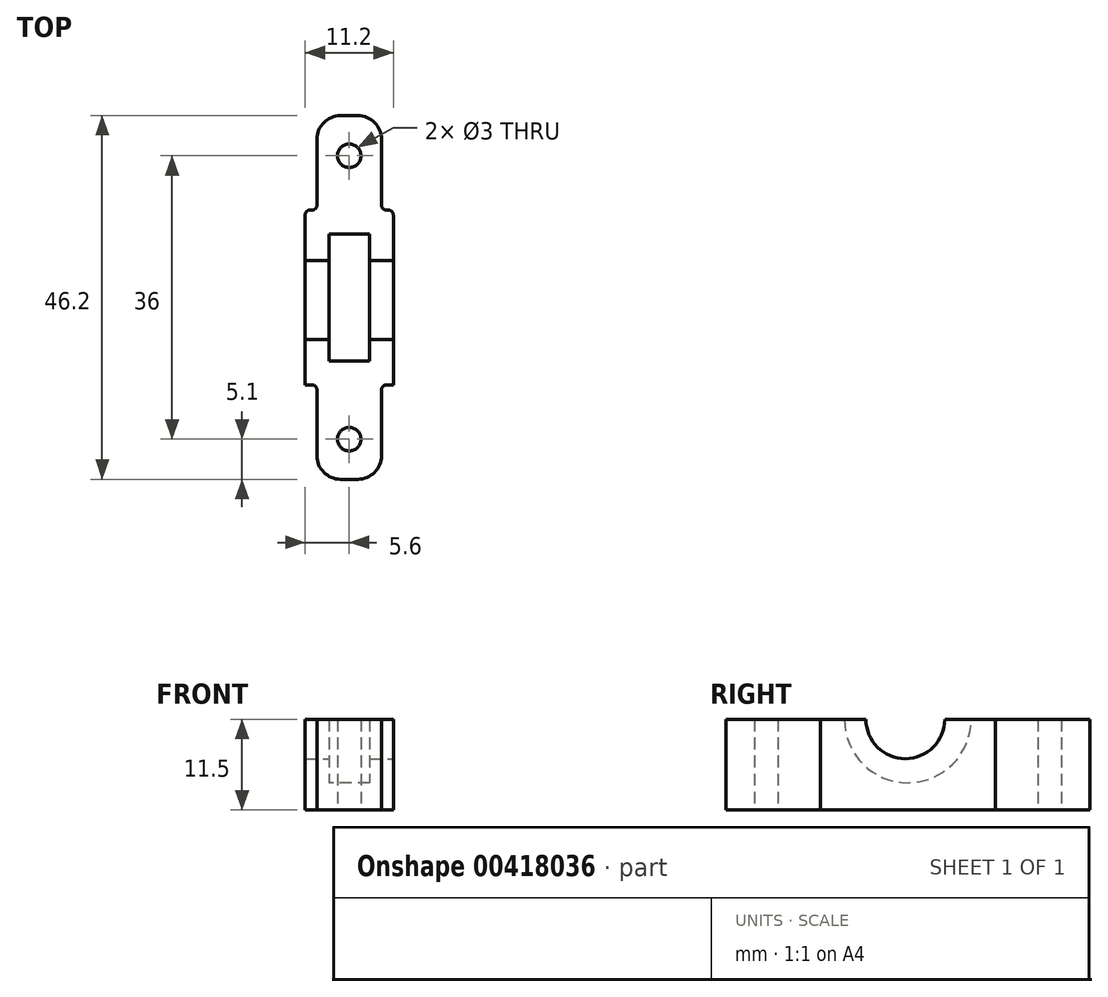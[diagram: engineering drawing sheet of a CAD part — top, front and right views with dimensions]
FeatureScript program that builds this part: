
annotation { "Feature Type Name" : "Feature", "Feature Type Description" : "" }
export const myFeature = defineFeature(function(context is Context, id is Id, definition is map)
    precondition{}
    {
        {
            var Q0;
            Q0=qCreatedBy(makeId("Top.planeOp"),FACE);
            var sketch = newSketch(context, id + "F0", { "sketchPlane" : qUnion([Q0])});
            skLineSegment(sketch, "E0", {"start": v(0, 0) * mm, "end": v(2.6, 0) * mm, "construction": true});
            skLineSegment(sketch, "E1", {"start": v(2.6, 0) * mm, "end": v(2.6, 8.1) * mm});
            skLineSegment(sketch, "E2", {"start": v(2.6, 8.1) * mm, "end": v(2.6, -8.1) * mm});
            skLineSegment(sketch, "E3.MirrorCS", {"start": v(-2.6, 8.1) * mm, "end": v(-2.6, -8.1) * mm});
            skLineSegment(sketch, "E4", {"start": v(2.6, 8.1) * mm, "end": v(-2.6, 8.1) * mm});
            skLineSegment(sketch, "E5", {"start": v(-2.6, -8.1) * mm, "end": v(2.6, -8.1) * mm});
            skLineSegment(sketch, "E6.0", {"start": v(4.97, 11.1) * mm, "end": v(4.73, 11.1) * mm});
            skLineSegment(sketch, "E6.1", {"start": v(5.6, 10.47) * mm, "end": v(5.6, -11.1) * mm});
            skLineSegment(sketch, "E6.2", {"start": v(-5.6, -11.1) * mm, "end": v(5.6, -11.1) * mm});
            skLineSegment(sketch, "E6.3", {"start": v(-5.6, 10.47) * mm, "end": v(-5.6, -11.1) * mm});
            skCircle(sketch, "E7", {"center": v(0, 18) * mm, "radius": 1.5 * mm});
            skLineSegment(sketch, "E8", {"start": v(-4.1, 11.73) * mm, "end": v(-4.1, 20.1) * mm});
            skLineSegment(sketch, "E9.MirrorCS", {"start": v(4.1, 11.73) * mm, "end": v(4.1, 20.1) * mm});
            skLineSegment(sketch, "E10", {"start": v(-1.1, 23.1) * mm, "end": v(1.1, 23.1) * mm});
            skLineSegment(sketch, "E11.trimOffspring", {"start": v(-4.73, 11.1) * mm, "end": v(-4.97, 11.1) * mm});
            skPoint(sketch, "E12.visualSharp", {"position": v(-4.1, 11.1) * mm});
            skArc(sketch, "E12.filletArc", {"start": v(-4.73, 11.1) * mm, "mid": v(-4.29, 11.29) * mm, "end": v(-4.1, 11.73) * mm});
            skPoint(sketch, "E13.visualSharp", {"position": v(-5.6, 11.1) * mm});
            skArc(sketch, "E13.filletArc", {"start": v(-4.97, 11.1) * mm, "mid": v(-5.41, 10.91) * mm, "end": v(-5.6, 10.47) * mm});
            skPoint(sketch, "E14.visualSharp", {"position": v(-4.1, 23.1) * mm});
            skArc(sketch, "E14.filletArc", {"start": v(-1.1, 23.1) * mm, "mid": v(-3.22, 22.22) * mm, "end": v(-4.1, 20.1) * mm});
            skArc(sketch, "E15.MirrorCS", {"start": v(1.1, 23.1) * mm, "mid": v(3.22, 22.22) * mm, "end": v(4.1, 20.1) * mm});
            skArc(sketch, "E16.MirrorCS", {"start": v(4.97, 11.1) * mm, "mid": v(5.41, 10.91) * mm, "end": v(5.6, 10.47) * mm});
            skArc(sketch, "E17.MirrorCS", {"start": v(4.73, 11.1) * mm, "mid": v(4.29, 11.29) * mm, "end": v(4.1, 11.73) * mm});
            skPoint(sketch, "E18.orphan", {"position": v(4.1, 11.1) * mm});
            skPoint(sketch, "E19.orphan", {"position": v(4.1, 23.1) * mm});
            skLineSegment(sketch, "E20.MirrorCS", {"start": v(-4.73, -11.1) * mm, "end": v(-4.97, -11.1) * mm});
            skArc(sketch, "E21.MirrorCS", {"start": v(-4.97, -11.1) * mm, "mid": v(-5.41, -10.91) * mm, "end": v(-5.6, -10.47) * mm});
            skLineSegment(sketch, "E22.MirrorCS", {"start": v(4.97, -11.1) * mm, "end": v(4.73, -11.1) * mm});
            skArc(sketch, "E23.MirrorCS", {"start": v(-4.73, -11.1) * mm, "mid": v(-4.29, -11.29) * mm, "end": v(-4.1, -11.73) * mm});
            skArc(sketch, "E24.MirrorCS", {"start": v(4.73, -11.1) * mm, "mid": v(4.29, -11.29) * mm, "end": v(4.1, -11.73) * mm});
            skArc(sketch, "E25.MirrorCS", {"start": v(4.97, -11.1) * mm, "mid": v(5.41, -10.91) * mm, "end": v(5.6, -10.47) * mm});
            skPoint(sketch, "E26.MirrorP", {"position": v(-4.1, -11.1) * mm});
            skPoint(sketch, "E27.MirrorP", {"position": v(-5.6, -11.1) * mm});
            skLineSegment(sketch, "E28.MirrorCS", {"start": v(4.1, -11.73) * mm, "end": v(4.1, -20.1) * mm});
            skLineSegment(sketch, "E29.MirrorCS", {"start": v(-4.1, -11.73) * mm, "end": v(-4.1, -20.1) * mm});
            skCircle(sketch, "E30.MirrorC", {"center": v(0, -18) * mm, "radius": 1.5 * mm});
            skArc(sketch, "E31.MirrorCS", {"start": v(1.1, -23.1) * mm, "mid": v(3.22, -22.22) * mm, "end": v(4.1, -20.1) * mm});
            skPoint(sketch, "E32.MirrorP", {"position": v(4.1, -23.1) * mm});
            skLineSegment(sketch, "E33.MirrorCS", {"start": v(-1.1, -23.1) * mm, "end": v(1.1, -23.1) * mm});
            skPoint(sketch, "E34.MirrorP", {"position": v(4.1, -11.1) * mm});
            skLineSegment(sketch, "E35.MirrorCS", {"start": v(2.6, -8.1) * mm, "end": v(-2.6, -8.1) * mm});
            skPoint(sketch, "E36.MirrorP", {"position": v(-4.1, -23.1) * mm});
            skArc(sketch, "E37.MirrorCS", {"start": v(-1.1, -23.1) * mm, "mid": v(-3.22, -22.22) * mm, "end": v(-4.1, -20.1) * mm});
            skLineSegment(sketch, "E38", {"start": v(-4.73, 11.1) * mm, "end": v(4.73, 11.1) * mm});
            skPoint(sketch, "E39.middle", {"position": v(0, 0) * mm});
            skLineSegment(sketch, "E40.bottom", {"start": v(-2.55, 8.05) * mm, "end": v(2.55, 8.05) * mm});
            skLineSegment(sketch, "E40.top", {"start": v(-2.55, -8.05) * mm, "end": v(2.55, -8.05) * mm});
            skLineSegment(sketch, "E40.left", {"start": v(-2.55, 8.05) * mm, "end": v(-2.55, -8.05) * mm});
            skLineSegment(sketch, "E40.right", {"start": v(2.55, 8.05) * mm, "end": v(2.55, -8.05) * mm});
            skSolve(sketch);
        }
        {
            var Q0;
            Q0 = qSketchRegion(id + "F0", true);
            var Q1;
            Q1=makeQuery(id+"F0.imprint","IMPRINT",FACE,{"disambiguationData":[TD([[makeQuery(id+"F0.imprint","IMPRINT",EDGE,{"derivedFrom":sQuery(id+"F0.wireOp",EDGE,"E40.bottom")}),-1.0]])]});
            var Q2;
            Q2=makeQuery(id+"F0.imprint","IMPRINT",FACE,{"disambiguationData":[TD([[makeQuery(id+"F0.imprint","IMPRINT",EDGE,{"derivedFrom":sQuery(id+"F0.wireOp",EDGE,"E3.MirrorCS")}),1.0]])]});
            extrude(context, id + "F1", {"entities" : qUnion([Q0, Q1, Q2]), "depth" : 11.5 * mm});
        }
        {
            var Q0;
            Q0=makeQuery(id+"F1.opExtrude","SWEPT_FACE",FACE,{"disambiguationData":[OSD([sQuery(id+"F0.wireOp",EDGE,"E6.1")])]});
            var sketch = newSketch(context, id + "F2", { "sketchPlane" : qUnion([Q0])});
            skLineSegment(sketch, "E41.0.0", {"start": v(10.47, 0) * mm, "end": v(10.47, 0) * mm});
            skLineSegment(sketch, "E41.0.1", {"start": v(10.47, 0) * mm, "end": v(10.47, 11.5) * mm});
            skLineSegment(sketch, "E41.0.2", {"start": v(10.47, 11.5) * mm, "end": v(10.47, 11.5) * mm});
            skLineSegment(sketch, "E41.0.3", {"start": v(10.47, 0) * mm, "end": v(10.47, 11.5) * mm});
            skCircle(sketch, "E42", {"center": v(-0.32, 11.5) * mm, "radius": 5 * mm});
            skSolve(sketch);
        }
        {
            var Q0;
            {var subQ0=sQuery(id+"F2.wireOp",EDGE,"E42");var subQ1=sQuery(id+"F2.wireOp",EDGE,"E41.0.2");var subQ2=makeQuery(id+"F2.imprint","INTERSECT",VERTEX,{"disambiguationData":[OD(0.0)],"derivedFrom":[subQ1,subQ0]});Q0=makeQuery(id+"F2.imprint","IMPRINT",FACE,{"disambiguationData":[TD([[makeQuery(id+"F2.imprint","IMPRINT",EDGE,{"disambiguationData":[TD([[subQ2,-1.0]])],"derivedFrom":subQ1}),1.0]])]});}
            var Q1;
            {var subQ0=sQuery(id+"F2.wireOp",EDGE,"E42");var subQ1=makeQuery(id+"F1.opExtrude","CAP_EDGE",EDGE,{"disambiguationData":[OSD([sQuery(id+"F0.wireOp",EDGE,"E6.1")])],"isStart":false});var subQ2=makeQuery(id+"F2.imprint","INTERSECT",VERTEX,{"disambiguationData":[OD(0.0)],"derivedFrom":[subQ1,subQ0]});Q1=makeQuery(id+"F2.imprint","IMPRINT",FACE,{"disambiguationData":[TD([[makeQuery(id+"F2.imprint","IMPRINT",EDGE,{"disambiguationData":[TD([[subQ2,1.0]])],"derivedFrom":subQ0}),1.0]])]});}
            extrude(context, id + "F3", {"entities" : qUnion([Q0, Q1]), "operationType" : NewBodyOperationType.REMOVE, "oppositeDirection" : true, "depth" : 25 * mm});
        }
        {
            var Q0;
            {var subQ0=sQuery(id+"F0.wireOp",EDGE,"E13.filletArc");var subQ1=sQuery(id+"F0.wireOp",EDGE,"E12.filletArc");var subQ2=sQuery(id+"F0.wireOp",EDGE,"E10");var subQ3=sQuery(id+"F0.wireOp",EDGE,"E9.MirrorCS");var subQ4=sQuery(id+"F0.wireOp",EDGE,"E8");var subQ5=sQuery(id+"F0.wireOp",EDGE,"E11.trimOffspring");var subQ6=sQuery(id+"F0.wireOp",EDGE,"E6.0");var subQ7=sQuery(id+"F0.wireOp",EDGE,"E6.1");var subQ8=sQuery(id+"F0.wireOp",EDGE,"E6.3");var subQ9=sQuery(id+"F0.wireOp",EDGE,"E7");var subQ10=sQuery(id+"F0.wireOp",EDGE,"E14.filletArc");var subQ11=sQuery(id+"F0.wireOp",EDGE,"E15.MirrorCS");var subQ12=sQuery(id+"F0.wireOp",EDGE,"E16.MirrorCS");var subQ13=sQuery(id+"F0.wireOp",EDGE,"E17.MirrorCS");Q0=makeQuery(id+"F3.boolean.opBoolean","SPLIT",FACE,{"disambiguationData":[TD([makeQuery(id+"F1.opExtrude","SWEPT_FACE",FACE,{"disambiguationData":[OSD([subQ6])]})])],"derivedFrom":makeQuery(id+"F1.opExtrude","CAP_FACE",FACE,{"disambiguationData":[OSD([subQ6,subQ7,sQuery(id+"F0.wireOp",EDGE,"E6.2"),subQ8,subQ9,subQ4,subQ3,subQ2,subQ5,subQ1,subQ0,subQ10,subQ11,subQ12,subQ13,sQuery(id+"F0.wireOp",EDGE,"E20.MirrorCS"),sQuery(id+"F0.wireOp",EDGE,"E22.MirrorCS"),sQuery(id+"F0.wireOp",EDGE,"E23.MirrorCS"),sQuery(id+"F0.wireOp",EDGE,"E24.MirrorCS"),sQuery(id+"F0.wireOp",EDGE,"E28.MirrorCS"),sQuery(id+"F0.wireOp",EDGE,"E29.MirrorCS"),sQuery(id+"F0.wireOp",EDGE,"E30.MirrorC"),sQuery(id+"F0.wireOp",EDGE,"E31.MirrorCS"),sQuery(id+"F0.wireOp",EDGE,"E33.MirrorCS"),sQuery(id+"F0.wireOp",EDGE,"E37.MirrorCS")])],"isStart":false})});}
            var sketch = newSketch(context, id + "F4", { "sketchPlane" : qUnion([Q0])});
            skLineSegment(sketch, "E43.0", {"start": v(-2.55, 8.05) * mm, "end": v(2.55, 8.05) * mm});
            skLineSegment(sketch, "E44.0", {"start": v(-2.55, 8.05) * mm, "end": v(-2.55, -8.05) * mm});
            skPoint(sketch, "E45.0", {"position": v(1.3, 0) * mm});
            skLineSegment(sketch, "E46.0", {"start": v(0, 0) * mm, "end": v(2.6, 0) * mm});
            skLineSegment(sketch, "E47.0", {"start": v(2.6, 8.1) * mm, "end": v(2.6, -8.1) * mm});
            skLineSegment(sketch, "E48.bottom", {"start": v(2.6, 0) * mm, "end": v(-2.55, 0) * mm});
            skLineSegment(sketch, "E48.top", {"start": v(2.6, 8.05) * mm, "end": v(-2.55, 8.05) * mm});
            skLineSegment(sketch, "E48.left", {"start": v(2.6, 0) * mm, "end": v(2.6, 8.05) * mm});
            skLineSegment(sketch, "E48.right", {"start": v(-2.55, 0) * mm, "end": v(-2.55, 8.05) * mm});
            skSolve(sketch);
        }
        {
            var Q0;
            {var subQ0=sQuery(id+"F4.wireOp",EDGE,"E48.right");var subQ1=sQuery(id+"F4.wireOp",EDGE,"E48.bottom");var subQ2=makeQuery(id+"F4.imprint","INTERSECT",VERTEX,{"derivedFrom":[subQ1,subQ0]});Q0=makeQuery(id+"F4.imprint","IMPRINT",FACE,{"disambiguationData":[TD([[makeQuery(id+"F4.imprint","IMPRINT",EDGE,{"disambiguationData":[TD([[subQ2,1.0]])],"derivedFrom":subQ1}),-1.0]])]});}
            var Q1;
            {var subQ1=sQuery(id+"F4.wireOp",EDGE,"E48.top");var subQ9=makeQuery(id+"F4.imprint","IMPRINT",VERTEX,{"derivedFrom":subQ1});Q1=makeQuery(id+"F4.imprint","IMPRINT",FACE,{"disambiguationData":[TD([[makeQuery(id+"F4.imprint","IMPRINT",EDGE,{"disambiguationData":[TD([[subQ9,1.0]])],"derivedFrom":subQ1}),1.0]])]});}
            var Q2;
            Q2=sQuery(id+"F4.wireOp",EDGE,"E48.bottom");
            revolve(context, id + "F5", {"operationType" : NewBodyOperationType.REMOVE, "entities" : qUnion([Q0, Q1]), "axis" : qUnion([Q2]), "revolveType" : RevolveType.FULL, "oppositeDirection" : true});
        }
    });
